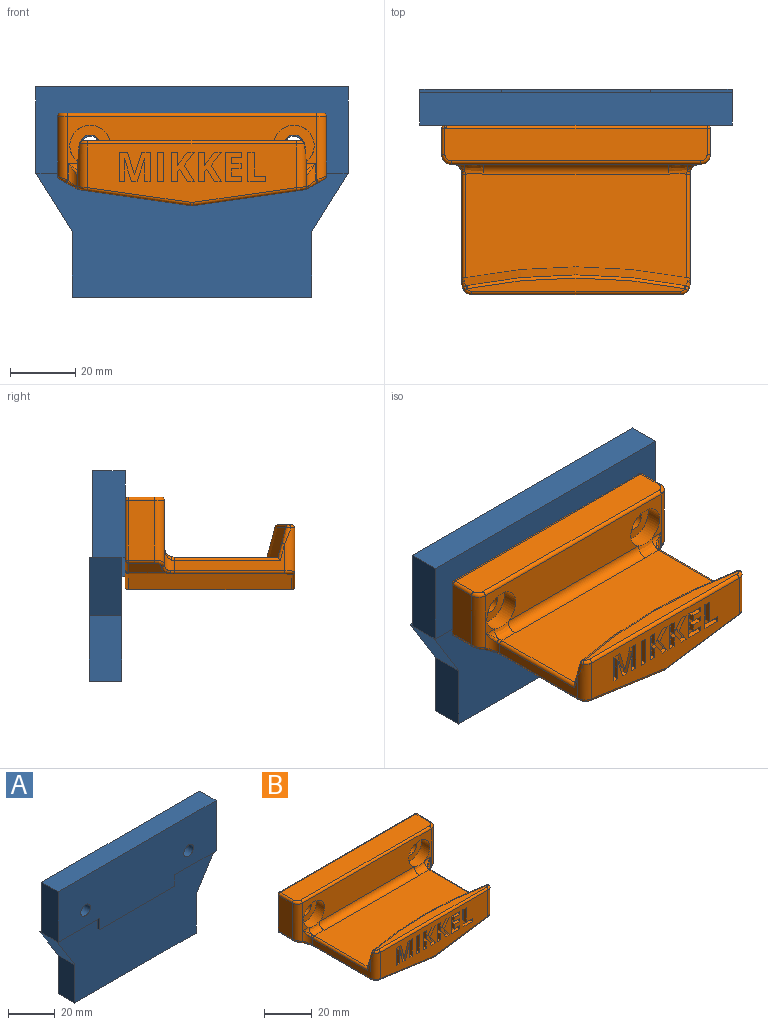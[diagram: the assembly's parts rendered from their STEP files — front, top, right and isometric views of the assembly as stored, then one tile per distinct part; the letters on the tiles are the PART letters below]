
ASSEMBLY  parts=2 mates=1
PART A: 24 faces, bbox 95.8x11x64.5 mm
  f0: plane 95.8x10mm, normal (0,0,1), area 958mm2, adj f1,f9,f10,f23
  f1: plane 26.5x10mm, normal (-1,0,0), area 265mm2, adj f0,f2,f10,f16,f23
  f2: plane 25x1mm, normal (0,0,-1), area 25mm2, adj f1,f3,f10,f22
  f3: plane 6x1mm, normal (-1,0,0), area 6mm2, adj f2,f4,f10,f22
  f4: plane 45.8x1mm, normal (0,0,-1), area 45.8mm2, adj f3,f5,f10,f22
  f5: plane 6x1mm, normal (1,0,0), area 6mm2, adj f4,f6,f10,f22
  f6: plane 25x1mm, normal (0,0,-1), area 25mm2, adj f5,f9,f10,f22
  f7: cylinder r=2.9mm len=10mm, axis (0,1,0), area 182.2mm2, adj f10,f23
  f8: cylinder r=2.9mm len=10mm, axis (0,1,0), area 182.2mm2, adj f10,f23
  f9: plane 26.5x10mm, normal (1,0,0), area 265mm2, adj f0,f6,f10,f20,f23
  f10: plane 95.8x32.5mm, normal (0,-1,0), area 2760.7mm2, adj f0,f1,f2,f3,f4,f5,f6,f7
  f11: plane 45.8x1mm, normal (0,0,1), area 45.8mm2, adj f12,f13,f21,f23
  f12: plane 6x1mm, normal (-1,0,0), area 6mm2, adj f11,f15,f21,f23
  f13: plane 6x1mm, normal (1,0,0), area 6mm2, adj f11,f14,f21,f23
  f14: plane 25x1mm, normal (0,0,1), area 25mm2, adj f13,f16,f21,f23
  f15: plane 25x1mm, normal (0,0,1), area 25mm2, adj f12,f20,f21,f23
  f16: plane 18x11.15mm, normal (-0.85,0,-0.53), area 211.7mm2, adj f1,f14,f17,f21,f22
  f17: plane 20x10mm, normal (-1,0,0), area 200mm2, adj f16,f18,f21,f22
  f18: plane 73.5x10mm, normal (0,0,-1), area 735mm2, adj f17,f19,f21,f22
  f19: plane 20x10mm, normal (1,0,0), area 200mm2, adj f18,f20,f21,f22
  f20: plane 18x11.15mm, normal (0.85,0,-0.53), area 211.7mm2, adj f9,f15,f19,f21,f22
  f21: plane 95.8x38mm, normal (0,1,0), area 2718.9mm2, adj f11,f12,f13,f14,f15,f16,f17,f18
  f22: plane 95.8x38mm, normal (0,-1,0), area 2718.9mm2, adj f2,f3,f4,f5,f6,f16,f17,f18
  f23: plane 95.8x32.5mm, normal (0,1,0), area 2760.7mm2, adj f0,f1,f7,f8,f9,f11,f12,f13
PART B: 164 faces, bbox 83x63.9x110 mm
  f0: plane 64x17.97mm, normal (0,-1,0), area 806mm2, adj f21,f28,f41,f43,f46,f89,f91,f92
  f1: plane 68x31.9mm, normal (0,0,1), area 2013.1mm2, adj f19,f25,f26,f27,f76,f78,f79,f81
  f2: plane 12.5x12.5mm, normal (0,-1,0), area 89.5mm2, adj f11,f15
  f3: plane 11.36x5.25mm, normal (-0.49,0,-0.87), area 60.6mm2, adj f30,f38,f40,f42,f44,f45
  f4: plane 50x34.02mm, normal (-0.14,0,-0.99), area 1706.1mm2, adj f30,f34,f35,f37,f39,f41,f54
  f5: plane 50x34.02mm, normal (0.14,0,-0.99), area 1706.1mm2, adj f22,f34,f46,f50,f55,f59,f62
  f6: plane 11.36x5.25mm, normal (0.49,0,-0.87), area 60.6mm2, adj f22,f66,f68,f69,f71,f72
  f7: plane 18.41x8mm, normal (1,0,0), area 147.3mm2, adj f32,f60,f67,f72
  f8: plane 80.5x10mm, normal (0,0,1), area 803.3mm2, adj f47,f51,f52,f56,f60,f61
  f9: cylinder r=3.25mm len=7mm, axis (0,-1,0), area 142.9mm2, adj f12,f13
  f10: plane 18.41x8mm, normal (-1,0,0), area 147.3mm2, adj f33,f44,f52,f53
  f11: cylinder r=3.25mm len=7mm, axis (0,-1,0), area 142.9mm2, adj f2,f12
  f12: plane 80.5x26.47mm, normal (0,1,0), area 1821.6mm2, adj f9,f11,f45,f49,f53,f54,f58,f61
  f13: plane 12.5x12.5mm, normal (0,-1,0), area 89.5mm2, adj f9,f14
  f14: cylinder r=6.25mm len=12.5mm, axis (0,1,0), area 196.3mm2, adj f13,f16,f27
  f15: cylinder r=6.25mm len=12.5mm, axis (0,1,0), area 196.3mm2, adj f2,f16,f25
  f16: plane 76.5x19.67mm, normal (0,-1,0), area 872.4mm2, adj f14,f15,f23,f24,f26,f29,f31,f32
  f17: plane 34x8.32mm, normal (-1,0,0), area 110.2mm2, adj f28,f31,f37,f81,f83
  f18: plane 34x8.32mm, normal (1,0,0), area 110.2mm2, adj f21,f23,f55,f78,f80
  f19: cone r=176.75mm half-angle=15deg, axis (0,0,-1), area 658.2mm2, adj f1,f78,f80,f81,f82,f83,f85,f86
  f20: plane 67.15x4.05mm, normal (0,0,1), area 198.2mm2, adj f86,f87,f89,f90
  f21: cylinder r=3mm len=13.42mm, axis (0,0,-1), area 57.8mm2, adj f0,f18,f50,f82,f87
  f22: cylinder r=3mm len=12.47mm, axis (0,-1,0), area 13.2mm2, adj f5,f6,f63,f65
  f23: cylinder r=3mm len=7.13mm, axis (0,0,-1), area 18.8mm2, adj f16,f18,f59,f63,f66,f73,f74,f76
  f24: cylinder r=3mm len=3.78mm, axis (1,0,0), area 7mm2, adj f16,f25,f73
  f25: bspline ~8.65x3.69mm, area 24.9mm2, adj f1,f15,f24,f26,f74
  f26: cylinder r=3mm len=56.56mm, axis (1,0,0), area 266.5mm2, adj f1,f16,f25,f27
  f27: bspline ~8.65x3.69mm, area 24.9mm2, adj f1,f14,f26,f29,f77
  f28: cylinder r=3mm len=13.42mm, axis (0,0,1), area 57.8mm2, adj f0,f17,f39,f85,f90
  f29: cylinder r=3mm len=3.78mm, axis (1,0,0), area 7mm2, adj f16,f27,f75
  f30: cylinder r=3mm len=12.47mm, axis (0,-1,0), area 13.2mm2, adj f3,f4,f36,f49
  f31: cylinder r=3mm len=7.13mm, axis (0,0,1), area 18.8mm2, adj f16,f17,f35,f36,f38,f75,f77,f79
  f32: cylinder r=3mm len=19.53mm, axis (0,0,1), area 89.4mm2, adj f7,f16,f56,f71
  f33: cylinder r=3mm len=19.53mm, axis (0,0,-1), area 89.4mm2, adj f10,f16,f42,f47
  f34: cylinder r=3mm len=50mm, axis (0,1,0), area 42.6mm2, adj f4,f5,f43,f58
  f35: bspline ~1.53x1.09mm, area 1.9mm2, adj f4,f31,f36,f37
  f36: bspline ~2.42x2.14mm, area 1.7mm2, adj f30,f31,f35,f38
  f37: cylinder r=1mm len=34mm, axis (0,1,0), area 48.6mm2, adj f4,f17,f35,f39
  f38: bspline ~3.98x3.1mm, area 4.6mm2, adj f3,f31,f36,f40
  f39: bspline ~3x3mm, area 6.1mm2, adj f4,f28,f37,f41
  f40: cylinder r=1mm len=1.01mm, axis (0.87,0,-0.49), area 0.5mm2, adj f3,f16,f38,f42
  f41: cylinder r=1mm len=31.86mm, axis (0.99,0,-0.14), area 50.3mm2, adj f0,f4,f39,f43
  f42: bspline ~3.52x3.18mm, area 5.3mm2, adj f3,f33,f40,f44
  f43: torus R=2mm, axis (0,-1,0), area 1.2mm2, adj f0,f34,f41,f46
  f44: cylinder r=1mm len=8mm, axis (0,-1,0), area 8.5mm2, adj f3,f10,f42,f48
  f45: cylinder r=1mm len=5.74mm, axis (-0.87,0,0.49), area 9.5mm2, adj f3,f12,f48,f49
  f46: cylinder r=1mm len=31.86mm, axis (0.99,0,0.14), area 50.3mm2, adj f0,f5,f43,f50
  f47: torus R=2mm, axis (0,0,-1), area 6.5mm2, adj f8,f33,f51,f52
  f48: sphere r=1mm, area 0.8mm2, adj f44,f45,f53
  f49: torus R=2mm, axis (0,-1,0), area 1.5mm2, adj f12,f30,f45,f54
  f50: bspline ~3.52x3.14mm, area 6.1mm2, adj f5,f21,f46,f55
  f51: cylinder r=1mm len=76.5mm, axis (-1,0,0), area 120.2mm2, adj f8,f16,f47,f56
  f52: cylinder r=1mm len=8mm, axis (0,1,0), area 12.6mm2, adj f8,f10,f47,f57
  f53: cylinder r=1mm len=18.41mm, axis (0,0,1), area 28.9mm2, adj f10,f12,f48,f57
  f54: cylinder r=1mm len=34.16mm, axis (-0.99,0,0.14), area 54mm2, adj f4,f12,f49,f58
  f55: cylinder r=1mm len=34mm, axis (0,-1,0), area 48.6mm2, adj f5,f18,f50,f59
  f56: torus R=2mm, axis (0,0,-1), area 6.5mm2, adj f8,f32,f51,f60
  f57: sphere r=1mm, area 2.1mm2, adj f52,f53,f61
  f58: torus R=2mm, axis (0,-1,0), area 1.2mm2, adj f12,f34,f54,f62
  f59: bspline ~1.53x1.09mm, area 1.9mm2, adj f5,f23,f55,f63
  f60: cylinder r=1mm len=8mm, axis (0,-1,0), area 12.6mm2, adj f7,f8,f56,f64
  f61: cylinder r=1mm len=80.5mm, axis (1,0,0), area 126.4mm2, adj f8,f12,f57,f64
  f62: cylinder r=1mm len=34.16mm, axis (-0.99,0,-0.14), area 54mm2, adj f5,f12,f58,f65
  f63: bspline ~2.16x2.02mm, area 1.7mm2, adj f22,f23,f59,f66
  f64: sphere r=1mm, area 1mm2, adj f60,f61,f67
  f65: torus R=2mm, axis (0,-1,0), area 1.5mm2, adj f12,f22,f62,f68
  f66: bspline ~3.98x3.1mm, area 4.6mm2, adj f6,f23,f63,f69
  f67: cylinder r=1mm len=18.41mm, axis (0,0,-1), area 28.9mm2, adj f7,f12,f64,f70
  f68: cylinder r=1mm len=5.74mm, axis (-0.87,0,-0.49), area 9.5mm2, adj f6,f12,f65,f70
  f69: cylinder r=1mm len=1.01mm, axis (0.87,0,0.49), area 0.5mm2, adj f6,f16,f66,f71
  f70: sphere r=1mm, area 0.8mm2, adj f67,f68,f72
  f71: bspline ~3.52x3.04mm, area 5.3mm2, adj f6,f32,f69,f72
  f72: cylinder r=1mm len=8mm, axis (0,-1,0), area 8.5mm2, adj f6,f7,f70,f71
  f73: bspline ~3.87x3.87mm, area 2.4mm2, adj f23,f24,f74
  f74: bspline ~1.79x1.28mm, area 1.4mm2, adj f23,f25,f73,f76
  f75: bspline ~3.87x3.87mm, area 2.4mm2, adj f29,f31,f77
  f76: torus R=4mm, axis (0,0,1), area 0mm2, adj f1,f23,f74,f78
  f77: bspline ~1.83x1.46mm, area 1.4mm2, adj f27,f31,f75,f79
  f78: cylinder r=1mm len=32.58mm, axis (0,-1,0), area 50.4mm2, adj f1,f18,f19,f76,f80
  f79: torus R=4mm, axis (0,0,1), area 0mm2, adj f1,f31,f77,f81
  f80: bspline ~109.96x30.92mm, area 6.9mm2, adj f18,f19,f78,f82
  f81: cylinder r=1mm len=32.58mm, axis (0,1,0), area 50.4mm2, adj f1,f17,f19,f79,f83
  f82: bspline ~6.94x3.28mm, area 8.7mm2, adj f19,f21,f80,f84
  f83: bspline ~109.96x30.92mm, area 6.9mm2, adj f17,f19,f81,f85
  f84: sphere r=1mm, area 2mm2, adj f82,f86,f87
  f85: bspline ~6.94x3.28mm, area 8.7mm2, adj f19,f28,f83,f88
  f86: torus R=173.3mm, axis (0,0,1), area 88.8mm2, adj f19,f20,f84,f88
  f87: torus R=2mm, axis (0,0,1), area 3.8mm2, adj f20,f21,f84,f89
  f88: sphere r=1mm, area 1.6mm2, adj f85,f86,f90
  f89: cylinder r=1mm len=64mm, axis (1,0,0), area 100.5mm2, adj f0,f20,f87,f90
  f90: torus R=2mm, axis (0,0,1), area 3.8mm2, adj f20,f28,f88,f89
  f91: plane 8.92x1.5mm, normal (1,0,0), area 13.4mm2, adj f0,f92,f96,f97
  f92: plane 5.51x1.5mm, normal (0,0,1), area 8.3mm2, adj f0,f91,f93,f97
  f93: plane 1.56x1.5mm, normal (-1,0,0), area 2.3mm2, adj f0,f92,f94,f97
  f94: plane 3.62x1.5mm, normal (0,0,-1), area 5.4mm2, adj f0,f93,f95,f97
  f95: plane 7.36x1.5mm, normal (-1,0,0), area 11mm2, adj f0,f94,f96,f97
  f96: plane 1.89x1.5mm, normal (0,0,-1), area 2.8mm2, adj f0,f91,f95,f97
  f97: plane 8.92x5.51mm, normal (0,-1,0), area 22.5mm2, adj f91,f92,f93,f94,f95,f96
  f98: plane 5.14x1.5mm, normal (0,0,1), area 7.7mm2, adj f0,f99,f109,f110
  f99: plane 1.56x1.5mm, normal (-1,0,0), area 2.3mm2, adj f0,f98,f100,f110
  f100: plane 3.25x1.5mm, normal (0,0,-1), area 4.9mm2, adj f0,f99,f101,f110
  f101: plane 2.3x1.5mm, normal (-1,0,0), area 3.5mm2, adj f0,f100,f102,f110
  f102: plane 3.02x1.5mm, normal (0,0,1), area 4.5mm2, adj f0,f101,f103,f110
  f103: plane 1.55x1.5mm, normal (-1,0,0), area 2.3mm2, adj f0,f102,f104,f110
  f104: plane 3.02x1.5mm, normal (0,0,-1), area 4.5mm2, adj f0,f103,f105,f110
  f105: plane 1.96x1.5mm, normal (-1,0,0), area 2.9mm2, adj f0,f104,f106,f110
  f106: plane 3.25x1.5mm, normal (0,0,1), area 4.9mm2, adj f0,f105,f107,f110
  f107: plane 1.55x1.5mm, normal (-1,0,0), area 2.3mm2, adj f0,f106,f108,f110
  f108: plane 5.14x1.5mm, normal (0,0,-1), area 7.7mm2, adj f0,f107,f109,f110
  f109: plane 8.92x1.5mm, normal (1,0,0), area 13.4mm2, adj f0,f98,f108,f110
  f110: plane 8.92x5.14mm, normal (0,-1,0), area 31.7mm2, adj f98,f99,f100,f101,f102,f103,f104,f105
  f111: plane 2.15x1.5mm, normal (0,0,1), area 3.2mm2, adj f0,f112,f123,f124
  f112: plane 4.97x3.14mm, normal (-0.85,0,-0.53), area 8.8mm2, adj f0,f111,f113,f124
  f113: plane 3.95x3.11mm, normal (-0.79,0,0.62), area 7.5mm2, adj f0,f112,f114,f124
  f114: plane 2.1x1.5mm, normal (0,0,-1), area 3.1mm2, adj f0,f113,f115,f124
  f115: plane 3.03x2.42mm, normal (0.78,0,-0.62), area 5.8mm2, adj f0,f114,f116,f124
  f116: plane 1.5x1.05mm, normal (0.82,0,-0.58), area 1.9mm2, adj f0,f115,f117,f124
  f117: plane 4.08x1.5mm, normal (-1,0,0), area 6.1mm2, adj f0,f116,f118,f124
  f118: plane 1.89x1.5mm, normal (0,0,-1), area 2.8mm2, adj f0,f117,f119,f124
  f119: plane 8.92x1.5mm, normal (1,0,0), area 13.4mm2, adj f0,f118,f120,f124
  f120: plane 1.89x1.5mm, normal (0,0,1), area 2.8mm2, adj f0,f119,f121,f124
  f121: plane 3.19x1.5mm, normal (-1,0,0), area 4.8mm2, adj f0,f120,f122,f124
  f122: plane 1.5x0.8mm, normal (-0.58,0,0.81), area 1.5mm2, adj f0,f121,f123,f124
  f123: plane 3.76x2.34mm, normal (0.85,0,0.53), area 6.6mm2, adj f0,f111,f122,f124
  f124: plane 8.92x7.18mm, normal (0,-1,0), area 36.5mm2, adj f111,f112,f113,f114,f115,f116,f117,f118
  f125: plane 2.15x1.5mm, normal (0,0,1), area 3.2mm2, adj f0,f126,f137,f138
  f126: plane 4.97x3.14mm, normal (-0.85,0,-0.53), area 8.8mm2, adj f0,f125,f127,f138
  f127: plane 3.95x3.11mm, normal (-0.79,0,0.62), area 7.5mm2, adj f0,f126,f128,f138
  f128: plane 2.1x1.5mm, normal (0,0,-1), area 3.1mm2, adj f0,f127,f129,f138
  f129: plane 3.03x2.42mm, normal (0.78,0,-0.62), area 5.8mm2, adj f0,f128,f130,f138
  f130: plane 1.5x1.05mm, normal (0.82,0,-0.58), area 1.9mm2, adj f0,f129,f131,f138
  f131: plane 4.08x1.5mm, normal (-1,0,0), area 6.1mm2, adj f0,f130,f132,f138
  f132: plane 1.89x1.5mm, normal (0,0,-1), area 2.8mm2, adj f0,f131,f133,f138
  f133: plane 8.92x1.5mm, normal (1,0,0), area 13.4mm2, adj f0,f132,f134,f138
  f134: plane 1.89x1.5mm, normal (0,0,1), area 2.8mm2, adj f0,f133,f135,f138
  f135: plane 3.19x1.5mm, normal (-1,0,0), area 4.8mm2, adj f0,f134,f136,f138
  f136: plane 1.5x0.8mm, normal (-0.58,0,0.81), area 1.5mm2, adj f0,f135,f137,f138
  f137: plane 3.76x2.34mm, normal (0.85,0,0.53), area 6.6mm2, adj f0,f125,f136,f138
  f138: plane 8.92x7.18mm, normal (0,-1,0), area 36.5mm2, adj f125,f126,f127,f128,f129,f130,f131,f132
  f139: plane 8.92x1.5mm, normal (1,0,0), area 13.4mm2, adj f0,f140,f142,f143
  f140: plane 1.89x1.5mm, normal (0,0,1), area 2.8mm2, adj f0,f139,f141,f143
  f141: plane 8.92x1.5mm, normal (-1,0,0), area 13.4mm2, adj f0,f140,f142,f143
  f142: plane 1.89x1.5mm, normal (0,0,-1), area 2.8mm2, adj f0,f139,f141,f143
  f143: plane 8.92x1.89mm, normal (0,-1,0), area 16.9mm2, adj f139,f140,f141,f142
  f144: plane 7x2.15mm, normal (0.96,0,0.29), area 11mm2, adj f0,f145,f162,f163
  f145: plane 1.73x1.5mm, normal (0,0,1), area 2.6mm2, adj f0,f144,f146,f163
  f146: plane 6.99x2.3mm, normal (-0.95,0,0.31), area 11mm2, adj f0,f145,f147,f163
  f147: plane 1.5x0.05mm, normal (0,0,1), area 0.1mm2, adj f0,f146,f148,f163
  f148: extruded ~2.07x1.5mm, area 3.1mm2, adj f0,f147,f149,f163
  f149: extruded ~1.5x0.69mm, area 1mm2, adj f0,f148,f150,f163
  f150: plane 4.22x1.5mm, normal (1,0,0), area 6.3mm2, adj f0,f149,f151,f163
  f151: plane 1.76x1.5mm, normal (0,0,1), area 2.6mm2, adj f0,f150,f152,f163
  f152: plane 8.92x1.5mm, normal (-1,0,0), area 13.4mm2, adj f0,f151,f153,f163
  f153: plane 2.57x1.5mm, normal (0,0,-1), area 3.9mm2, adj f0,f152,f154,f163
  f154: plane 6.82x2.24mm, normal (0.95,0,-0.31), area 10.8mm2, adj f0,f153,f155,f163
  f155: plane 1.5x0.04mm, normal (0,0,-1), area 0.1mm2, adj f0,f154,f156,f163
  f156: plane 6.82x2.11mm, normal (-0.96,0,-0.3), area 10.7mm2, adj f0,f155,f157,f163
  f157: plane 2.58x1.5mm, normal (0,0,-1), area 3.9mm2, adj f0,f156,f158,f163
  f158: plane 8.92x1.5mm, normal (1,0,0), area 13.4mm2, adj f0,f157,f159,f163
  f159: plane 1.69x1.5mm, normal (0,0,1), area 2.5mm2, adj f0,f158,f160,f163
  f160: plane 4.15x1.5mm, normal (-1,0,0), area 6.2mm2, adj f0,f159,f161,f163
  f161: extruded ~2.85x1.5mm, area 4.3mm2, adj f0,f160,f162,f163
  f162: plane 1.5x0.05mm, normal (0,0,1), area 0.1mm2, adj f0,f144,f161,f163
  f163: plane 9.54x8.92mm, normal (0,-1,0), area 54.9mm2, adj f144,f145,f146,f147,f148,f149,f150,f151
PLACE A t=(0,-3,0)mm
PLACE B t=(0,-11,-8)mm
MATE fastened B.f11 <-> A.f8  axis (0,1,0) through (31.25,-4,-18)mm
